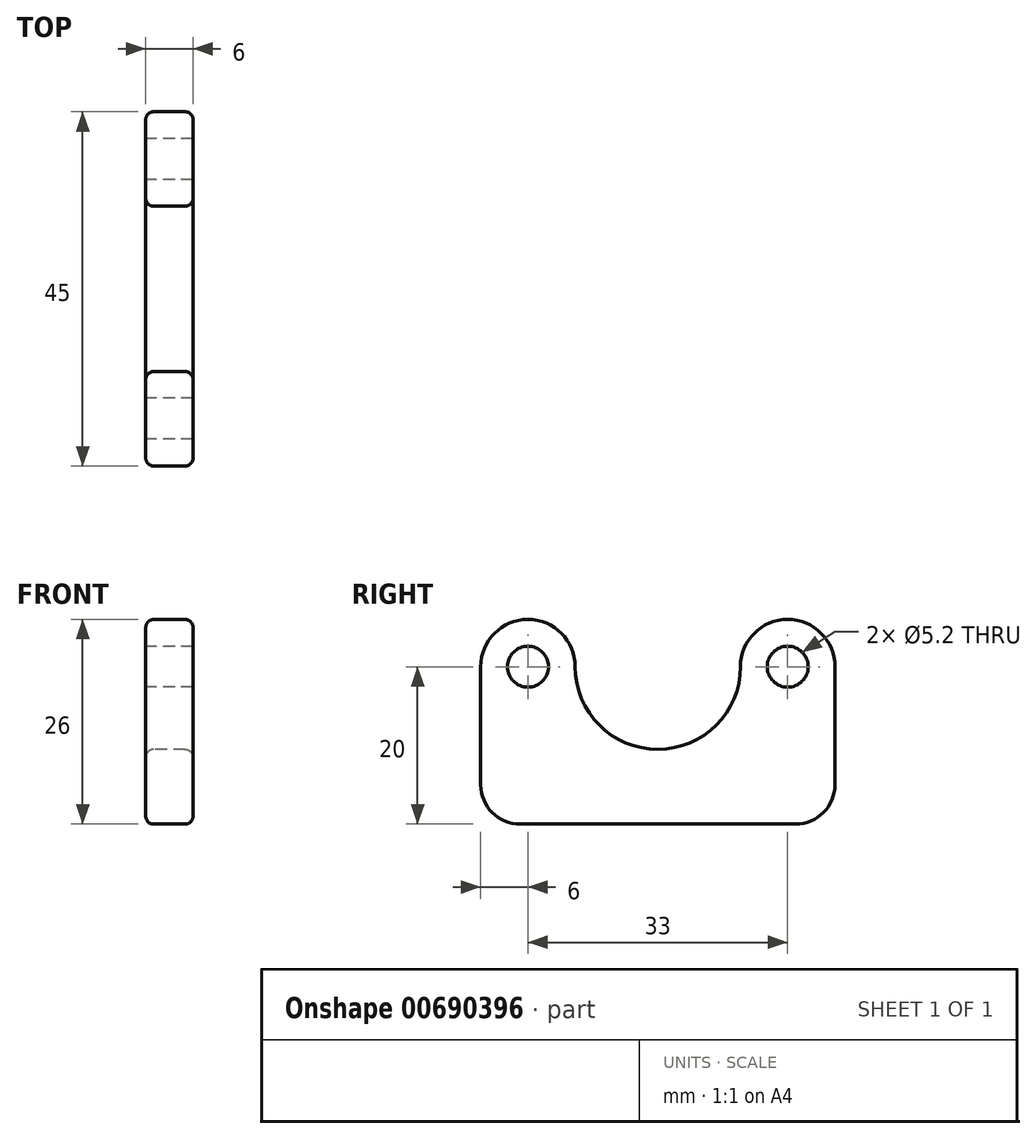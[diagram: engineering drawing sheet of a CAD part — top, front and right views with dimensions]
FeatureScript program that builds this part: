
annotation { "Feature Type Name" : "Feature", "Feature Type Description" : "" }
export const myFeature = defineFeature(function(context is Context, id is Id, definition is map)
    precondition{}
    {
        {
            var Q0;
            Q0=qCreatedBy(makeId("Right.planeOp"),FACE);
            var sketch = newSketch(context, id + "F0", { "sketchPlane" : qUnion([Q0])});
            skCircle(sketch, "E0", {"center": v(0, 0) * mm, "radius": 16.5 * mm, "construction": true});
            skCircle(sketch, "E1", {"center": v(-16.5, 0) * mm, "radius": 2.6 * mm});
            skCircle(sketch, "E2", {"center": v(16.5, 0) * mm, "radius": 2.6 * mm});
            skArc(sketch, "E3", {"start": v(-10.5, 0) * mm, "mid": v(-16.5, 6) * mm, "end": v(-22.5, 0) * mm});
            skArc(sketch, "E4", {"start": v(22.5, 0) * mm, "mid": v(16.5, 6) * mm, "end": v(10.5, 0) * mm});
            skArc(sketch, "E5", {"start": v(-10.5, 0) * mm, "mid": v(0, -10.5) * mm, "end": v(10.5, 0) * mm});
            skLineSegment(sketch, "E6.top", {"start": v(-17.5, -20) * mm, "end": v(17.5, -20) * mm});
            skLineSegment(sketch, "E6.left", {"start": v(-22.5, 0) * mm, "end": v(-22.5, -15) * mm});
            skLineSegment(sketch, "E6.right", {"start": v(22.5, 0) * mm, "end": v(22.5, -15) * mm});
            skPoint(sketch, "E7.visualSharp", {"position": v(-22.5, -20) * mm});
            skArc(sketch, "E7.filletArc", {"start": v(-22.5, -15) * mm, "mid": v(-21.04, -18.54) * mm, "end": v(-17.5, -20) * mm});
            skPoint(sketch, "E8.visualSharp", {"position": v(22.5, -20) * mm});
            skArc(sketch, "E8.filletArc", {"start": v(17.5, -20) * mm, "mid": v(21.04, -18.54) * mm, "end": v(22.5, -15) * mm});
            skSolve(sketch);
        }
        {
            var Q0;
            Q0=makeQuery(id+"F0.imprint","IMPRINT",FACE,{"disambiguationData":[TD([[makeQuery(id+"F0.imprint","IMPRINT",EDGE,{"derivedFrom":sQuery(id+"F0.wireOp",EDGE,"E1")}),-1.0]])]});
            extrude(context, id + "F1", {"entities" : qUnion([Q0]), "depth" : 6 * mm, "offsetDistance" : 25 * mm});
        }
        {
            var Q0;
            Q0=makeQuery(id+"F1.opExtrude","CAP_EDGE",EDGE,{"disambiguationData":[OSD([sQuery(id+"F0.wireOp",EDGE,"E6.left")])],"isStart":false});
            var Q1;
            Q1=makeQuery(id+"F1.opExtrude","CAP_EDGE",EDGE,{"disambiguationData":[OSD([sQuery(id+"F0.wireOp",EDGE,"E6.left")])],"isStart":true});
            fillet(context, id + "F2", {"entities" : qUnion([Q0, Q1]), "radius" : 1 * mm, "tangentPropagation" : true, "allowEdgeOverflow" : false});
        }
    });
